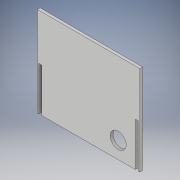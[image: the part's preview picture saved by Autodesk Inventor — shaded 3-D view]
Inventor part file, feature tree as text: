
AUTODESK INVENTOR PART (.ipt)
format: ipt  version: 2018 (Build 220112000, 112)  size: 105,472 bytes
history: native  units: in
note: dims shown in document units (in); Inventor stores cm internally (conversion verified against a paired STEP export)
features: extrude x1, sketch x1
ambient origin geometry x8: Origin, YZ Plane, XZ Plane, XY Plane, X Axis, Y Axis, Z Axis, Center Point
bodies: Solid1 (feature_tree)
feature tree (2):
  extrude  "Extrusion1"  Depth=0.2188in
  sketch  "Sketch1"  dims[d0=8.0in d7=1.25in d8=0.2188in d9=0.0in]
